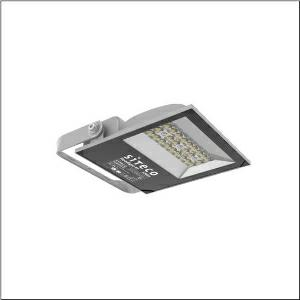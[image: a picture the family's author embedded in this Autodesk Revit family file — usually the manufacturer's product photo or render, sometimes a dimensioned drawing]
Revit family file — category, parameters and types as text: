
# Revit family: floodlight_fl_41_mini___pl32_5xa8571a2121_f875
name_source: partatom
category: Lighting Fixtures
units: mm (PartAtom-declared; Revit-internal decimal feet)

## family parameters
Cut with Voids When Loaded = No
Host = Face
Light Source = No
Part Type = Normal
Room Calculation Point = No
Round Connector Dimension = Use Diameter
Shared = No

## types (1)
- --- (1 x LED, 13000 lm, 100 W, 4000K)
    Apparent Load = 100 VA
    CIE Flux Codes = 40 79 99 100 100
    Color Rendering = 70
    Color Temperature = 4000K
    Default Elevation = 1800 mm
    Description = Floodlight FL 41 mini, floodlight, primary light control with lens, of PMMA, primary optical cover: protective disc, transparent, light distribution: PL32, light emission: direct distribution, installation type: surface-mounted, LED, High Power LED, rated luminous flux: 13.000lm, luminous efficacy: 130lm/W, light colour: 740, colour temperature: 4000K, control gear: ON/OFF Multilumen, with cable, 3x 1.5mm², mains connection: 220..240V, AC, 50/60Hz, connection cable pre-assembled, cable length: 2m, rated input power: 100W, luminaire housing, of diecast aluminium, powder-coated, metallic grey (RAL 9006), length: 265mm, width: 245mm, height: 54mm, protection rating (complete): IP65, insulation class (complete): insulation class I (protective earthing), certification: CE, ENEC, impact resistance: IK08, permissible operating ambient temperature: -40..+40°C, permissible storage temperature: -40..+60°C, packaging unit: 1 piece

Light Distribution: PL32
    Height = 54 mm
    Lamp = 1 x LED
    Lamp Light Flux = 13000 lm
    Lamp Power = 100 W
    Lamp count = 1
    Length = 226 mm
    Luminous efficacy = 130 lm/W
    Manufacturer = Siteco
    ModVariant = No
    Model = 5XA8571A2121
    Mounting Place = Ceiling
    Mounting Type = Surface mounted
    Number of Poles = 1
    OnlyDefault = Yes
    Power Factor = 1
    Product Name = Floodlight FL 41 mini | PL32
    Product group = floodlight | ceiling mounted
    ProductGroupID = 305
    Protection Class = Protection class I
    Protection Degree = IP 65
    RLX_Detail_Level = 1
    RLX_Emergency_Light_Flux = 0 lm
    RLX_Emergency_Type = 0
    RLX_Emergency_Type_DB = No
    RlxData = <blob elided: 24641 chars, md5=83982084>
    Socket = socket
    Standby Power = 0 W
    System Light Flux = 13000 lm
    System Power = 100 W
    Type Comments = factory setting: luminous flux: 100 % | (OFF | OFF | OFF)
    Type Image = l_1248226.jpg
    URL = http://relux.com
    VarID = @adj_131209
    Voltage = 0 V
    Weight = 0.00 kg
    Width = 241 mm

## geometry (parser evidence)
native form markers: Blend x4, Sweep x9
no freeform markers — native parametric forms only
